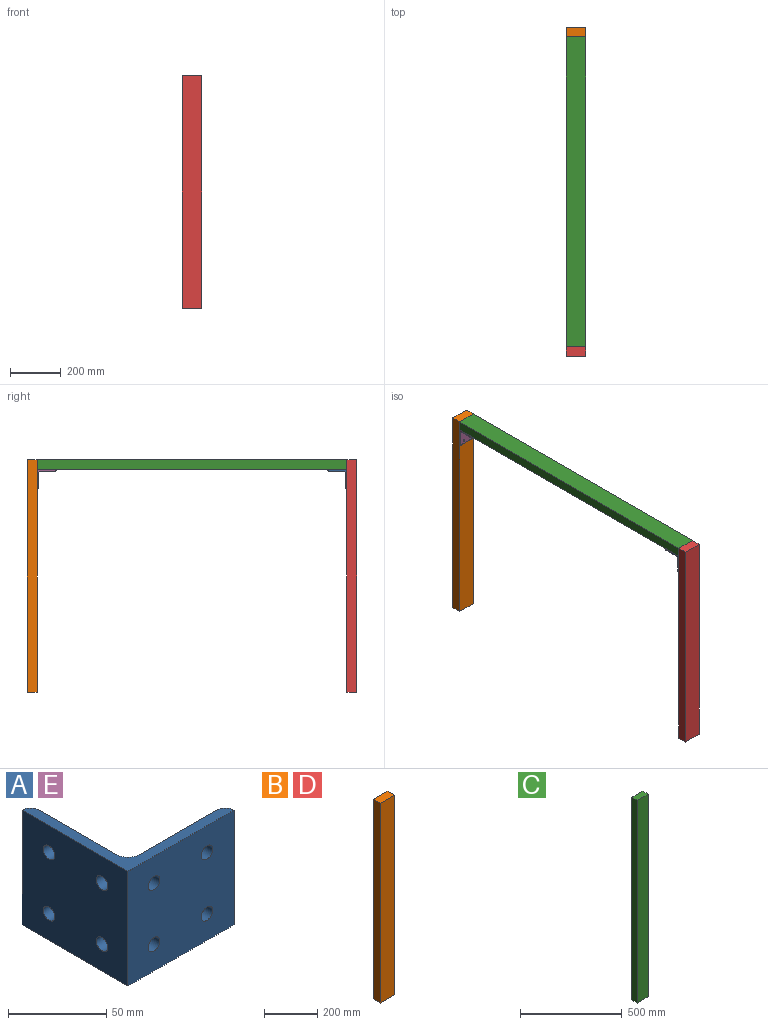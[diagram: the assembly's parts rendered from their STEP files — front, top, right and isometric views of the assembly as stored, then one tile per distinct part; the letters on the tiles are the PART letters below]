
ASSEMBLY  parts=5 mates=12
PART A: 17 faces, bbox 76.2x76.2x71.4 mm
  f0: plane 71.37x55.58mm, normal (1,0,0), area 3748.6mm2, adj f5,f6,f7,f8,f13,f14,f15,f16
  f1: plane 76.2x71.37mm, normal (-1,0,0), area 5220.6mm2, adj f2,f6,f7,f8,f13,f14,f15,f16
  f2: plane 76.2x71.37mm, normal (0,-1,0), area 5220.6mm2, adj f1,f4,f7,f8,f9,f10,f11,f12
  f3: plane 71.37x55.58mm, normal (0,1,0), area 3748.6mm2, adj f4,f5,f7,f8,f9,f10,f11,f12
  f4: cylinder r=6.35mm len=71.37mm, axis (0,0,-1), area 711.9mm2, adj f2,f3,f7,f8
  f5: cylinder r=7.92mm len=71.37mm, axis (0,0,-1), area 888.5mm2, adj f0,f3,f7,f8
  f6: cylinder r=6.35mm len=71.37mm, axis (0,0,-1), area 711.9mm2, adj f0,f1,f7,f8
  f7: plane 76.2x76.2mm, normal (0,0,1), area 923.6mm2, adj f0,f1,f2,f3,f4,f5,f6
  f8: plane 76.2x76.2mm, normal (0,0,-1), area 923.6mm2, adj f0,f1,f2,f3,f4,f5,f6
  f9: cylinder r=4.17mm len=8.33mm, axis (0,-1,0), area 166.2mm2, adj f2,f3
  f10: cylinder r=4.17mm len=8.33mm, axis (0,-1,0), area 166.2mm2, adj f2,f3
  f11: cylinder r=4.17mm len=8.33mm, axis (0,-1,0), area 166.2mm2, adj f2,f3
  f12: cylinder r=4.17mm len=8.33mm, axis (0,-1,0), area 166.2mm2, adj f2,f3
  f13: cylinder r=4.17mm len=8.33mm, axis (-1,0,0), area 166.2mm2, adj f0,f1
  f14: cylinder r=4.17mm len=8.33mm, axis (-1,0,0), area 166.2mm2, adj f0,f1
  f15: cylinder r=4.17mm len=8.33mm, axis (-1,0,0), area 166.2mm2, adj f0,f1
  f16: cylinder r=4.17mm len=8.33mm, axis (-1,0,0), area 166.2mm2, adj f0,f1
PART B: 6 faces, bbox 76.2x38.1x914.4 mm
  f0: plane 914.4x38.1mm, normal (-1,0,0), area 34838.6mm2, adj f1,f3,f4,f5
  f1: plane 914.4x76.2mm, normal (0,-1,0), area 69677.3mm2, adj f0,f2,f4,f5
  f2: plane 914.4x38.1mm, normal (1,0,0), area 34838.6mm2, adj f1,f3,f4,f5
  f3: plane 914.4x76.2mm, normal (0,1,0), area 69677.3mm2, adj f0,f2,f4,f5
  f4: plane 76.2x38.1mm, normal (0,0,-1), area 2903.2mm2, adj f0,f1,f2,f3
  f5: plane 76.2x38.1mm, normal (0,0,1), area 2903.2mm2, adj f0,f1,f2,f3
PART C: 6 faces, bbox 76.2x38.1x1219.2 mm
  f0: plane 1219.2x38.1mm, normal (-1,0,0), area 46451.5mm2, adj f1,f3,f4,f5
  f1: plane 1219.2x76.2mm, normal (0,-1,0), area 92903mm2, adj f0,f2,f4,f5
  f2: plane 1219.2x38.1mm, normal (1,0,0), area 46451.5mm2, adj f1,f3,f4,f5
  f3: plane 1219.2x76.2mm, normal (0,1,0), area 92903mm2, adj f0,f2,f4,f5
  f4: plane 76.2x38.1mm, normal (0,0,-1), area 2903.2mm2, adj f0,f1,f2,f3
  f5: plane 76.2x38.1mm, normal (0,0,1), area 2903.2mm2, adj f0,f1,f2,f3
PART D: same geometry as B
PART E: same geometry as A
PLACE A rot(axis=(-0.58,-0.58,0.58),120deg) t=(112.46,-1759.59,523.22)mm
PLACE B t=(76.77,-540.39,561.32)mm
PLACE C rot(axis=(0,-0.71,0.71),180deg) t=(152.97,-1759.59,561.32)mm
PLACE D rot(axis=(1,0,0),180deg) t=(76.77,-1759.59,-353.08)mm
PLACE E rot(axis=(-0.58,0.58,-0.58),120deg) t=(112.46,-540.39,523.22)mm
MATE planar D.f0 <-> C.f2  axis (-1,0,0) through (76.77,-1778.64,104.12)mm
MATE planar E.f2 <-> C.f3  axis (0,0,1) through (112.46,-578.5,523.22)mm
MATE planar B.f0 <-> C.f2  axis (-1,0,0) through (76.77,-540.39,561.32)mm
MATE planar A.f7 <-> C.f2  axis (-1,0,0) through (76.77,-1759.59,523.22)mm
MATE planar A.f1 <-> D.f1  axis (0,-1,0) through (112.46,-1759.59,485.1)mm
MATE planar D.f1 <-> C.f5  axis (0,1,0) through (114.87,-1759.59,104.12)mm
MATE planar A.f2 <-> C.f3  axis (0,0,1) through (112.46,-1721.47,523.22)mm
MATE planar E.f4 <-> C.f2  axis (-1,0,0) through (76.77,-610.24,523.22)mm
MATE planar C.f1 <-> B.f5  axis (0,0,1) through (114.87,-1149.99,561.32)mm
MATE planar E.f1 <-> B.f1  axis (0,1,0) through (112.46,-540.39,485.1)mm
MATE planar C.f4 <-> B.f1  axis (0,1,0) through (114.87,-540.39,542.27)mm
MATE planar C.f1 <-> D.f4  axis (0,0,1) through (114.87,-1149.99,561.32)mm
